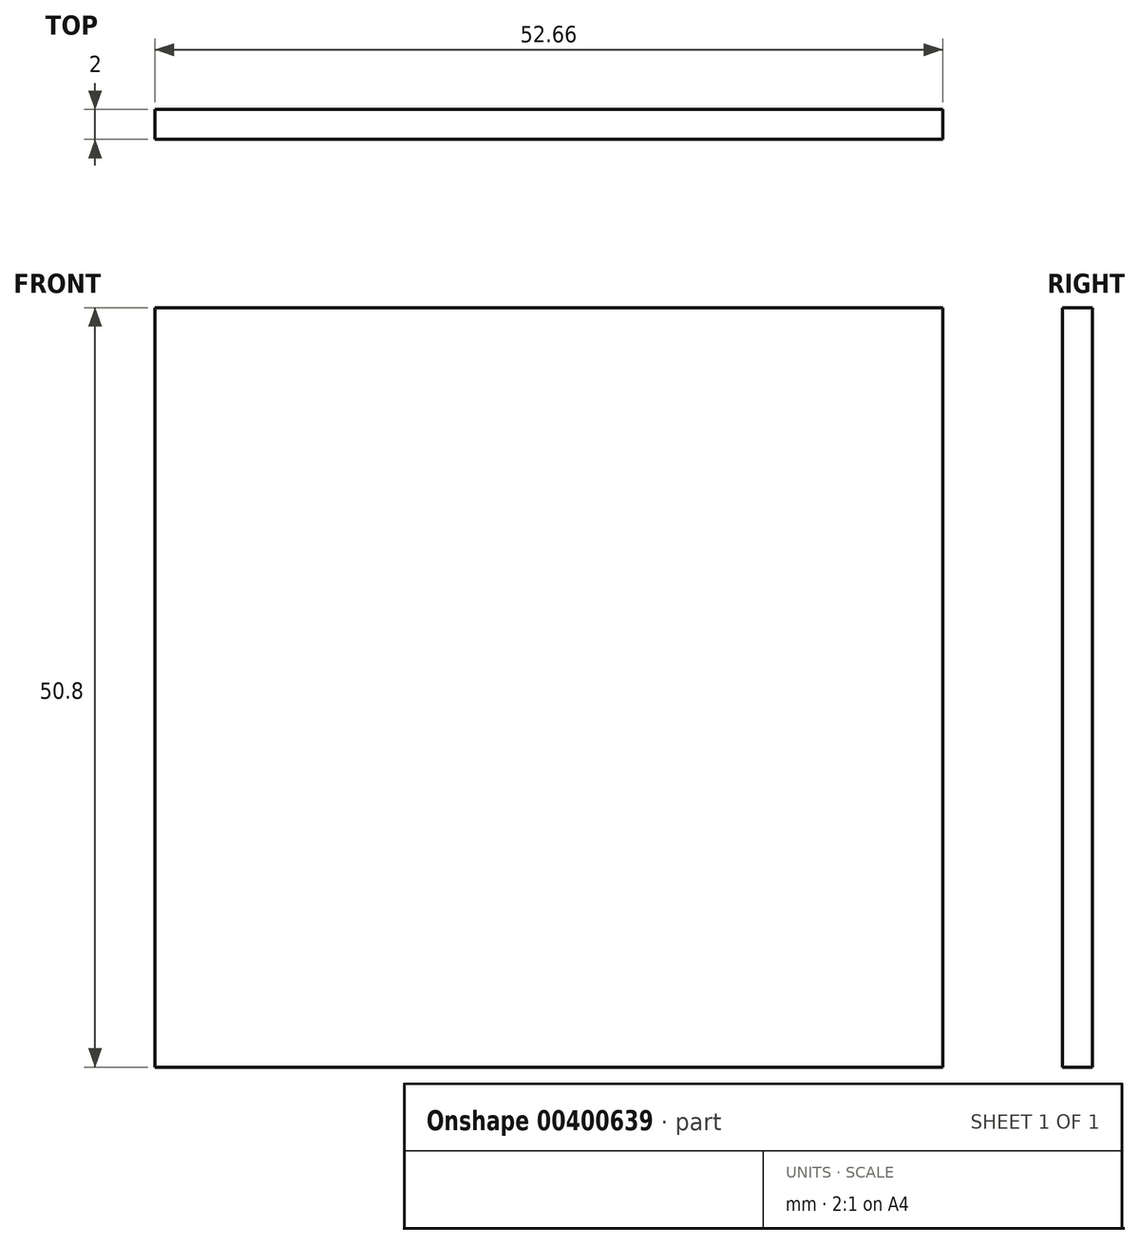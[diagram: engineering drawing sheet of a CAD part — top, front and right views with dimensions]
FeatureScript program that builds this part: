
annotation { "Feature Type Name" : "Feature", "Feature Type Description" : "" }
export const myFeature = defineFeature(function(context is Context, id is Id, definition is map)
    precondition{}
    {
        {
            var Q0;
            Q0=qCreatedBy(makeId("Right.planeOp"),FACE);
            var sketch = newSketch(context, id + "F0", { "sketchPlane" : qUnion([Q0])});
            skPoint(sketch, "E0.right.end.orphan", {"position": v(0, 12.17) * mm});
            skLineSegment(sketch, "E1.bottom", {"start": v(-14.78, 54.71) * mm, "end": v(-12.78, 54.71) * mm});
            skLineSegment(sketch, "E1.top", {"start": v(-14.78, 3.91) * mm, "end": v(-12.78, 3.91) * mm});
            skLineSegment(sketch, "E1.left", {"start": v(-14.78, 54.71) * mm, "end": v(-14.78, 3.91) * mm});
            skLineSegment(sketch, "E1.right", {"start": v(-12.78, 54.71) * mm, "end": v(-12.78, 3.91) * mm});
            skSolve(sketch);
        }
        {
            var Q0;
            Q0 = qSketchRegion(id + "F0", true);
            extrude(context, id + "F1", {"entities" : qUnion([Q0]), "depth" : 52.65 * mm, "symmetric" : true});
        }
    });
